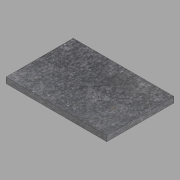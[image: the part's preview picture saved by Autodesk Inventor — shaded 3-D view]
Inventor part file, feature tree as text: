
AUTODESK INVENTOR PART (.ipt)
format: ipt  version: 2022.2 (Build 262287000, 287)  size: 110,592 bytes
history: native  units: in
note: dims shown in document units (in); Inventor stores cm internally (conversion verified against a paired STEP export)
features: other x1, extrude x1, sketch x1
ambient origin geometry x8: Origin, YZ Plane, XZ Plane, XY Plane, X Axis, Y Axis, Z Axis, Center Point
bodies: Body1 (feature_tree)
feature tree (3):
  other  "24x36x2-50"
  extrude  "Extrusion2"  Depth=24.0in
  sketch  "Sketch3"  dims[d4=36.0in d5=24.0in d6=2.0in d7=0.0in]
